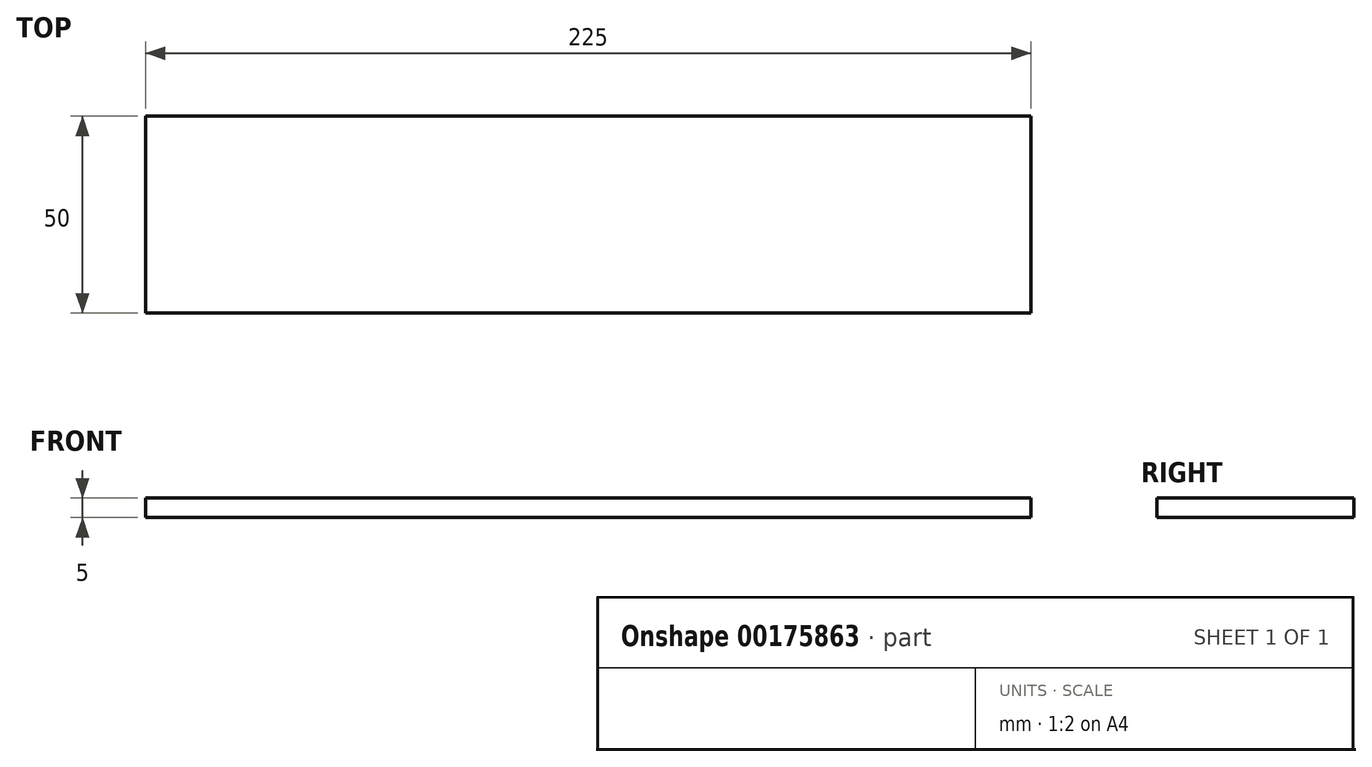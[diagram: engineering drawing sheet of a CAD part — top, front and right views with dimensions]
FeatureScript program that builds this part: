
annotation { "Feature Type Name" : "Feature", "Feature Type Description" : "" }
export const myFeature = defineFeature(function(context is Context, id is Id, definition is map)
    precondition{}
    {
        {
            var Q0;
            Q0=qCreatedBy(makeId("Top.planeOp"),FACE);
            var sketch = newSketch(context, id + "F0", { "sketchPlane" : qUnion([Q0])});
            skLineSegment(sketch, "E0.bottom", {"start": v(-120.49, 14.4) * mm, "end": v(104.51, 14.4) * mm});
            skLineSegment(sketch, "E0.top", {"start": v(-120.49, -35.6) * mm, "end": v(104.51, -35.6) * mm});
            skLineSegment(sketch, "E0.left", {"start": v(-120.49, 14.4) * mm, "end": v(-120.49, -35.6) * mm});
            skLineSegment(sketch, "E0.right", {"start": v(104.51, 14.4) * mm, "end": v(104.51, -35.6) * mm});
            skSolve(sketch);
        }
        {
            var Q0;
            Q0 = qSketchRegion(id + "F0", true);
            extrude(context, id + "F1", {"entities" : qUnion([Q0]), "depth" : 5 * mm});
        }
    });
